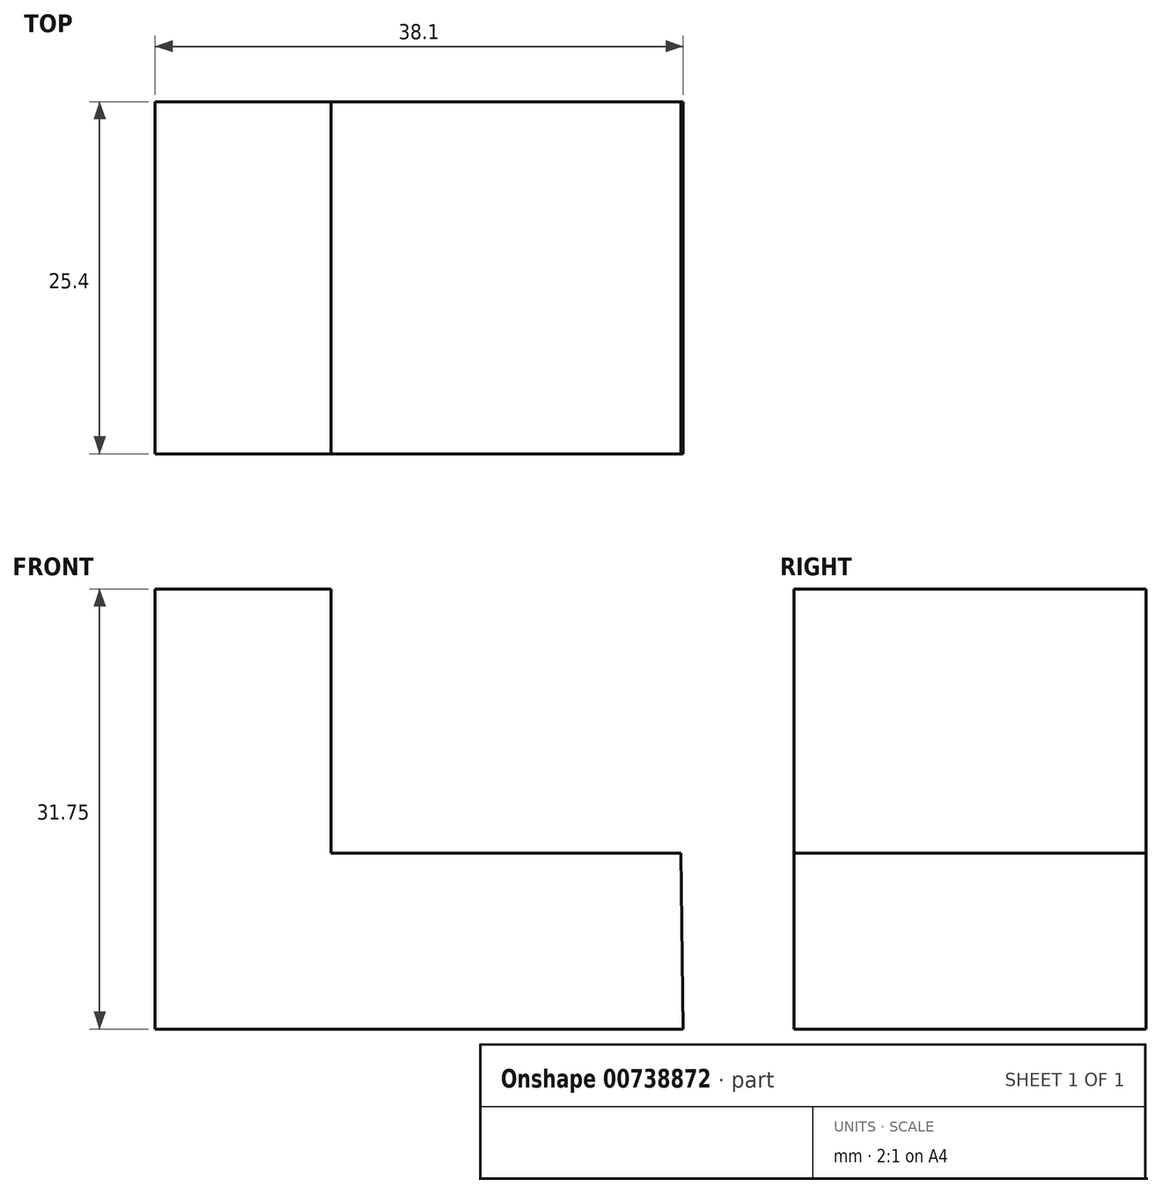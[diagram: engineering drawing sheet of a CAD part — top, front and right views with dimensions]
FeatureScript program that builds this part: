
annotation { "Feature Type Name" : "Feature", "Feature Type Description" : "" }
export const myFeature = defineFeature(function(context is Context, id is Id, definition is map)
    precondition{}
    {
        {
            var Q0;
            Q0=qCreatedBy(makeId("Front.planeOp"),FACE);
            var sketch = newSketch(context, id + "F0", { "sketchPlane" : qUnion([Q0])});
            skLineSegment(sketch, "E0", {"start": v(0, 0) * mm, "end": v(38.1, 0) * mm});
            skLineSegment(sketch, "E1", {"start": v(0, 0) * mm, "end": v(0, 31.75) * mm});
            skLineSegment(sketch, "E2", {"start": v(0, 31.75) * mm, "end": v(12.7, 31.75) * mm});
            skLineSegment(sketch, "E3", {"start": v(12.7, 31.75) * mm, "end": v(12.7, 12.7) * mm});
            skLineSegment(sketch, "E4", {"start": v(12.7, 12.7) * mm, "end": v(37.93, 12.7) * mm});
            skLineSegment(sketch, "E5", {"start": v(37.93, 12.7) * mm, "end": v(38.1, 0) * mm});
            skSolve(sketch);
        }
        {
            var Q0;
            Q0 = qSketchRegion(id + "F0", true);
            extrude(context, id + "F1", {"entities" : qUnion([Q0]), "depth" : 25.4 * mm, "offsetDistance" : 25.4 * mm});
        }
    });
